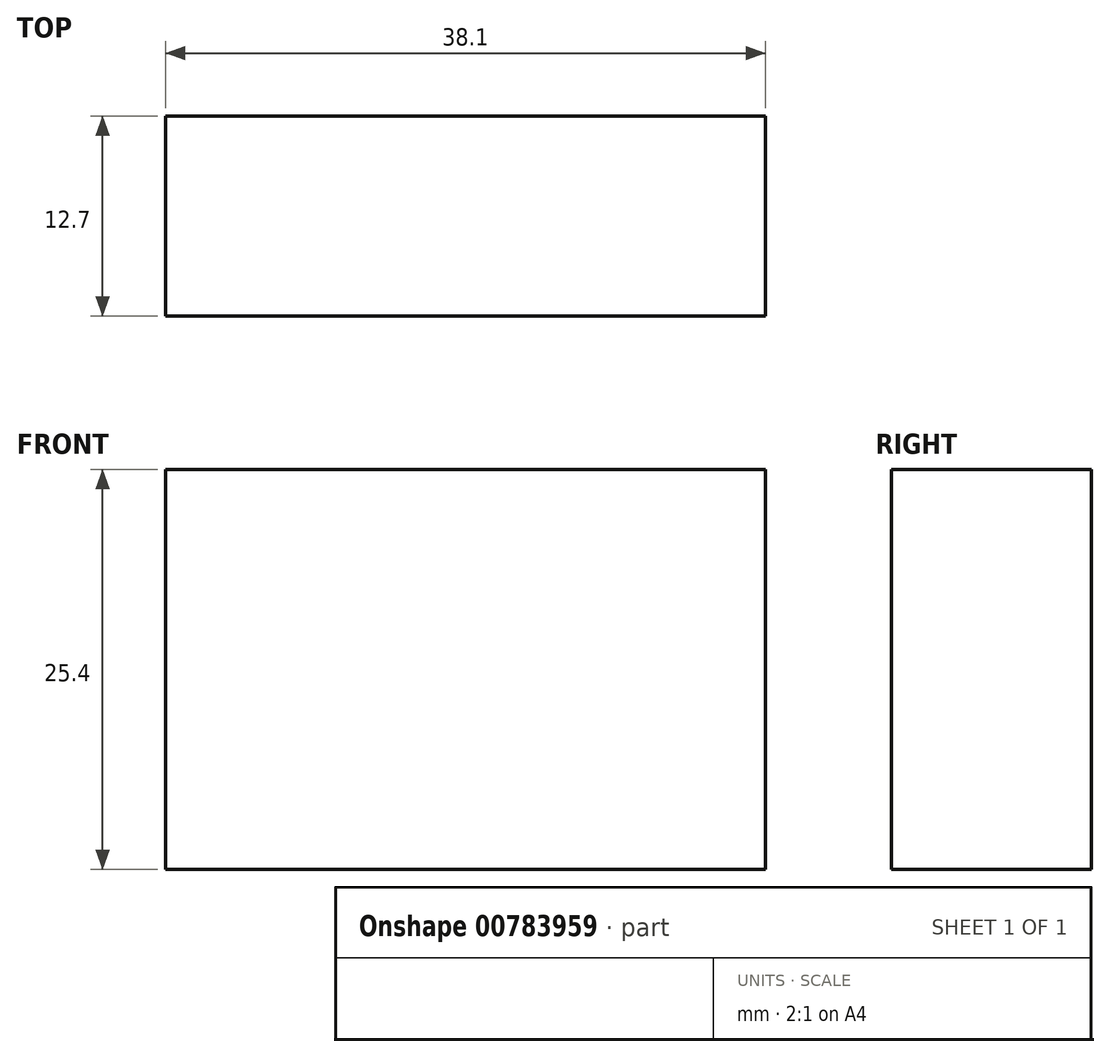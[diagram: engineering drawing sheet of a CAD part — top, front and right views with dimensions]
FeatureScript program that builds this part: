
annotation { "Feature Type Name" : "Feature", "Feature Type Description" : "" }
export const myFeature = defineFeature(function(context is Context, id is Id, definition is map)
    precondition{}
    {
        {
            var Q0;
            Q0=qCreatedBy(makeId("Top.planeOp"),FACE);
            var sketch = newSketch(context, id + "F0", { "sketchPlane" : qUnion([Q0])});
            skLineSegment(sketch, "E0", {"start": v(0, 0) * mm, "end": v(38.1, 0) * mm});
            skLineSegment(sketch, "E1", {"start": v(38.1, 0) * mm, "end": v(38.1, -12.7) * mm});
            skLineSegment(sketch, "E2", {"start": v(38.1, -12.7) * mm, "end": v(0, -12.7) * mm});
            skLineSegment(sketch, "E3", {"start": v(0, -12.7) * mm, "end": v(0, 0) * mm});
            skSolve(sketch);
        }
        {
            var Q0;
            Q0 = qSketchRegion(id + "F0", true);
            extrude(context, id + "F1", {"entities" : qUnion([Q0]), "depth" : 25.4 * mm, "offsetDistance" : 25.4 * mm});
        }
    });
